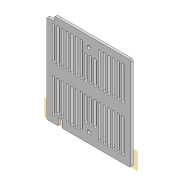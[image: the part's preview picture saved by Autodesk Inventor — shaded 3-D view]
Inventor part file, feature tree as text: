
AUTODESK INVENTOR PART (.ipt)
format: ipt  version: 2020 (Build 240168000, 168)  size: 670,208 bytes
history: native  units: mm
features: other x10, extrude x8, sketch x8, fillet x3, mirror x1
ambient origin geometry x8: Origin, YZ Plane, XZ Plane, XY Plane, X Axis, Y Axis, Z Axis, Center Point
bodies: Body1 (feature_tree)
feature tree (30):
  other  "Sólido1"
  other  "Plano de trabalho1"
  extrude  "Extrusão1"  Depth=0.5mm
  extrude  "Extrusão2"  Depth=1.0mm
  fillet  "Arredondamento1"  Radius=0.5mm
  extrude  "Extrusão3"  Depth=4.5mm
  extrude  "Extrusão4"  Depth=4.5mm
  fillet  "Arredondamento2"  Radius=10.0mm
  extrude  "Extrusão5"  Depth=18.0mm
  mirror  "Espelhamento1"
  extrude  "Extrusão6"  Depth=23.0mm
  extrude  "Extrusão7"  Depth=42.0mm
  fillet  "Arredondamento3"  Radius=42.0mm
  extrude  "Extrusão8"  Depth=1.0mm
  sketch  "Esboço1"  dims[d0=0.5mm d1=0.5mm]
  other  "Referência1"
  other  "Referência2"
  sketch  "Esboço2"  dims[d2=1.0mm d3=1.0mm d4=0.5mm]
  sketch  "Esboço3"  dims[d5=0.5mm d6=4.5mm]
  other  "Contorno projetado1"
  other  "Contorno projetado2"
  sketch  "Esboço4"  dims[d7=0.5mm d8=4.5mm d9=10.0mm]
  sketch  "Esboço5"  dims[d10=10.0mm d11=18.0mm]
  sketch  "Esboço6"  dims[d12=23.0mm d13=23.0mm]
  sketch  "Esboço7"  dims[d14=31.0mm d15=42.0mm d16=42.0mm]
  sketch  "Esboço8"  dims[d17=31.0mm d18=31.0mm d19=3.2mm d20=3.2mm d21=70.0mm d23=6.0mm d24=10.0mm d26=10.0mm d28=2.2mm d29=0.0mm d30=3.2mm d31=6.0mm d32=30.0mm d34=6.0mm d35=10.0mm d37=10.0mm d39=3.2mm d40=6.0mm d41=50.0mm d43=6.0mm d44=10.0mm d46=10.0mm d48=20.0mm d50=6.0mm d51=10.0mm d53=10.0mm d55=14.0mm d56=14.0mm d57=3.0mm d58=0.0mm d59=2.2mm d60=8.0mm d61=0.0mm d62=3.0mm d63=100.0mm d64=0.0mm d65=2.0mm d66=10.0mm d67=20.0mm d68=0.0mm d69=0.0mm d70=19.8mm d71=9.5mm d72=5.0mm d73=2.0mm d74=0.0mm d75=3.0mm d76=0.0mm d77=10.0mm d78=6.0mm d79=1.0mm d80=0.8mm d81=0.0mm]
  other  "Contorno projetado3"
  other  "Calorímetro.iam"
  other  "suporte_fechamento:2"
  other  "suporte_fechamento:3"
